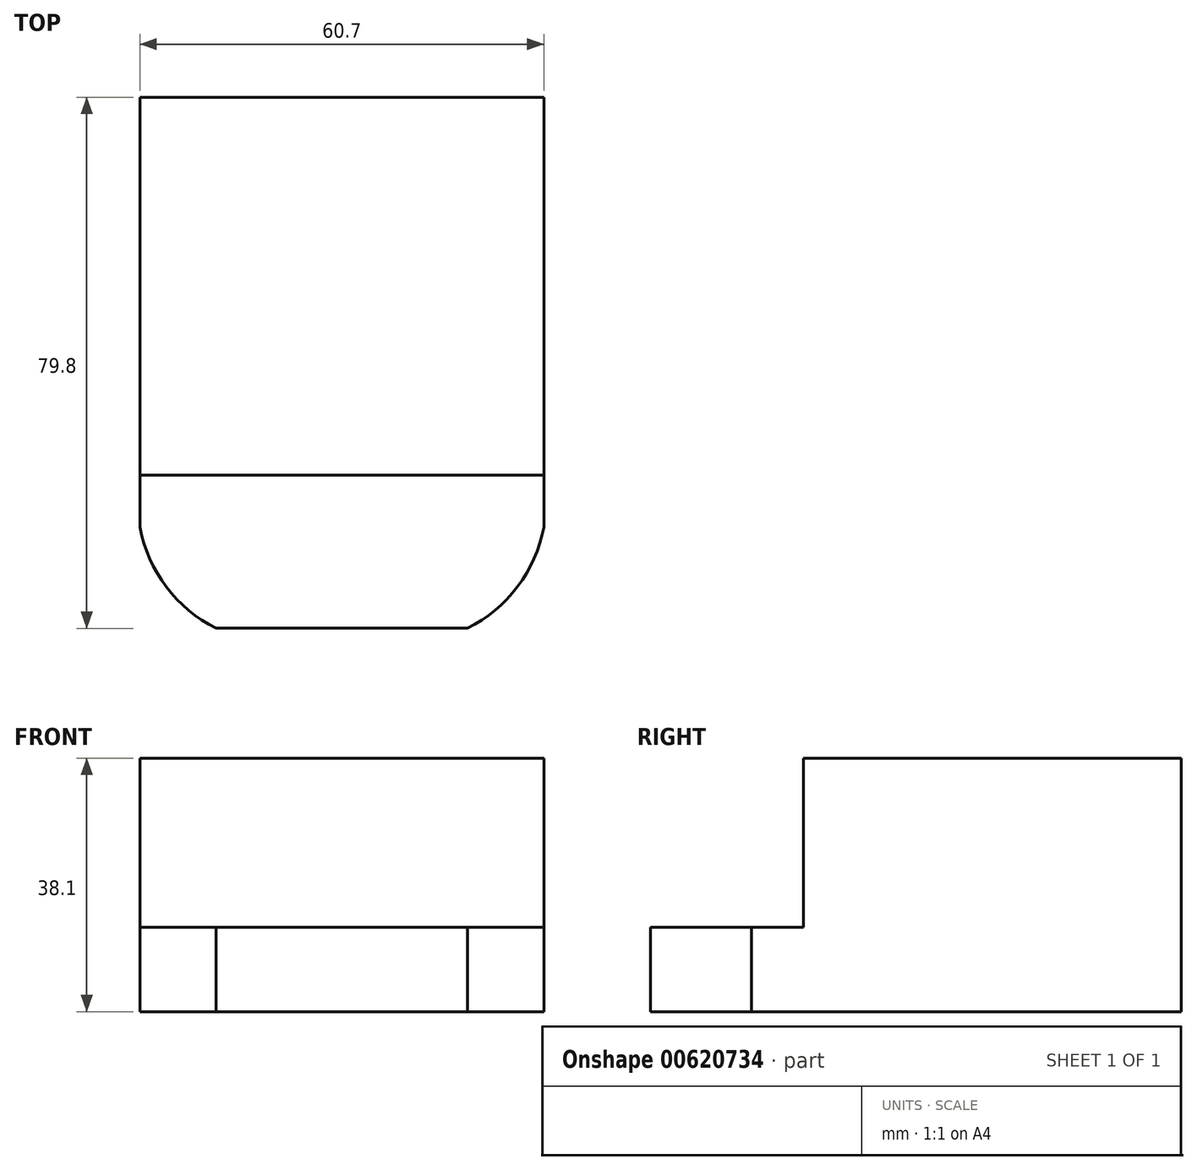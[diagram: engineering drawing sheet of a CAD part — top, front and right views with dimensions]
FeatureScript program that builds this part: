
annotation { "Feature Type Name" : "Feature", "Feature Type Description" : "" }
export const myFeature = defineFeature(function(context is Context, id is Id, definition is map)
    precondition{}
    {
        {
            var Q0;
            Q0=qCreatedBy(makeId("Top.planeOp"),FACE);
            var sketch = newSketch(context, id + "F0", { "sketchPlane" : qUnion([Q0])});
            skLineSegment(sketch, "E0.bottom", {"start": v(-30.35, 39.9) * mm, "end": v(30.35, 39.9) * mm});
            skLineSegment(sketch, "E0.top", {"start": v(-30.35, -39.9) * mm, "end": v(30.35, -39.9) * mm});
            skLineSegment(sketch, "E0.left", {"start": v(-30.35, 39.9) * mm, "end": v(-30.35, -39.9) * mm});
            skLineSegment(sketch, "E0.right", {"start": v(30.35, 39.9) * mm, "end": v(30.35, -39.9) * mm});
            skPoint(sketch, "E0.middle", {"position": v(0, 0) * mm});
            skSolve(sketch);
        }
        {
            var Q0;
            Q0=makeQuery(id+"F0.imprint","IMPRINT",FACE,{"disambiguationData":[TD([[makeQuery(id+"F0.imprint","IMPRINT",EDGE,{"derivedFrom":sQuery(id+"F0.wireOp",EDGE,"E0.bottom")}),-1.0]])]});
            extrude(context, id + "F1", {"entities" : qUnion([Q0]), "depth" : 12.7 * mm, "offsetDistance" : 25.4 * mm});
        }
        {
            var Q0;
            Q0=makeQuery(id+"F1.opExtrude","CAP_FACE",FACE,{"disambiguationData":[OSD([sQuery(id+"F0.wireOp",EDGE,"E0.bottom"),sQuery(id+"F0.wireOp",EDGE,"E0.top"),sQuery(id+"F0.wireOp",EDGE,"E0.left"),sQuery(id+"F0.wireOp",EDGE,"E0.right")])],"isStart":false});
            var sketch = newSketch(context, id + "F2", { "sketchPlane" : qUnion([Q0])});
            skLineSegment(sketch, "E1.bottom", {"start": v(-30.35, 39.9) * mm, "end": v(30.35, 39.9) * mm});
            skLineSegment(sketch, "E1.top", {"start": v(-30.35, -16.89) * mm, "end": v(30.35, -16.89) * mm});
            skLineSegment(sketch, "E1.left", {"start": v(-30.35, 39.9) * mm, "end": v(-30.35, -16.89) * mm});
            skLineSegment(sketch, "E1.right", {"start": v(30.35, 39.9) * mm, "end": v(30.35, -16.89) * mm});
            skSolve(sketch);
        }
        {
            var Q0;
            Q0=makeQuery(id+"F2.imprint","IMPRINT",FACE,{"disambiguationData":[TD([[makeQuery(id+"F2.imprint","IMPRINT",EDGE,{"derivedFrom":sQuery(id+"F2.wireOp",EDGE,"E1.bottom")}),-1.0]])]});
            extrude(context, id + "F3", {"entities" : qUnion([Q0]), "operationType" : NewBodyOperationType.ADD, "depth" : 25.4 * mm, "offsetDistance" : 25.4 * mm});
        }
        {
            var Q0;
            Q0=makeQuery(id+"F1.opExtrude","CAP_FACE",FACE,{"disambiguationData":[OSD([sQuery(id+"F0.wireOp",EDGE,"E0.bottom"),sQuery(id+"F0.wireOp",EDGE,"E0.top"),sQuery(id+"F0.wireOp",EDGE,"E0.left"),sQuery(id+"F0.wireOp",EDGE,"E0.right")])],"isStart":false});
            var sketch = newSketch(context, id + "F4", { "sketchPlane" : qUnion([Q0])});
            skArc(sketch, "E2", {"start": v(-30.35, -16.89) * mm, "mid": v(-28.47, -30.32) * mm, "end": v(-18.87, -39.9) * mm});
            skArc(sketch, "E3.MirrorCS", {"start": v(30.35, -16.89) * mm, "mid": v(28.47, -30.32) * mm, "end": v(18.87, -39.9) * mm});
            skLineSegment(sketch, "E4", {"start": v(-30.35, -16.89) * mm, "end": v(-30.35, -39.9) * mm});
            skLineSegment(sketch, "E5", {"start": v(18.87, -39.9) * mm, "end": v(30.35, -39.9) * mm});
            skLineSegment(sketch, "E6", {"start": v(30.35, -39.9) * mm, "end": v(30.35, -16.89) * mm});
            skSolve(sketch);
        }
        {
            var Q0;
            {var subQ0=sQuery(id+"F4.wireOp",EDGE,"E5");Q0=makeQuery(id+"F4.imprint","IMPRINT",FACE,{"disambiguationData":[TD([[makeQuery(id+"F4.imprint","IMPRINT",EDGE,{"derivedFrom":subQ0}),1.0]])]});}
            var Q1;
            {var subQ0=sQuery(id+"F4.wireOp",EDGE,"E2");var subQ1=makeQuery(id+"F1.opExtrude","CAP_EDGE",EDGE,{"disambiguationData":[OSD([sQuery(id+"F0.wireOp",EDGE,"E0.top")])],"isStart":false});var subQ2=makeQuery(id+"F4.imprint","INTERSECT",VERTEX,{"derivedFrom":[subQ1,subQ0]});Q1=makeQuery(id+"F4.imprint","IMPRINT",FACE,{"disambiguationData":[TD([[makeQuery(id+"F4.imprint","IMPRINT",EDGE,{"disambiguationData":[TD([[subQ2,1.0]])],"derivedFrom":subQ0}),-1.0]])]});}
            extrude(context, id + "F5", {"entities" : qUnion([Q0, Q1]), "operationType" : NewBodyOperationType.REMOVE, "oppositeDirection" : true, "depth" : 25.4 * mm, "offsetDistance" : 25.4 * mm});
        }
    });
